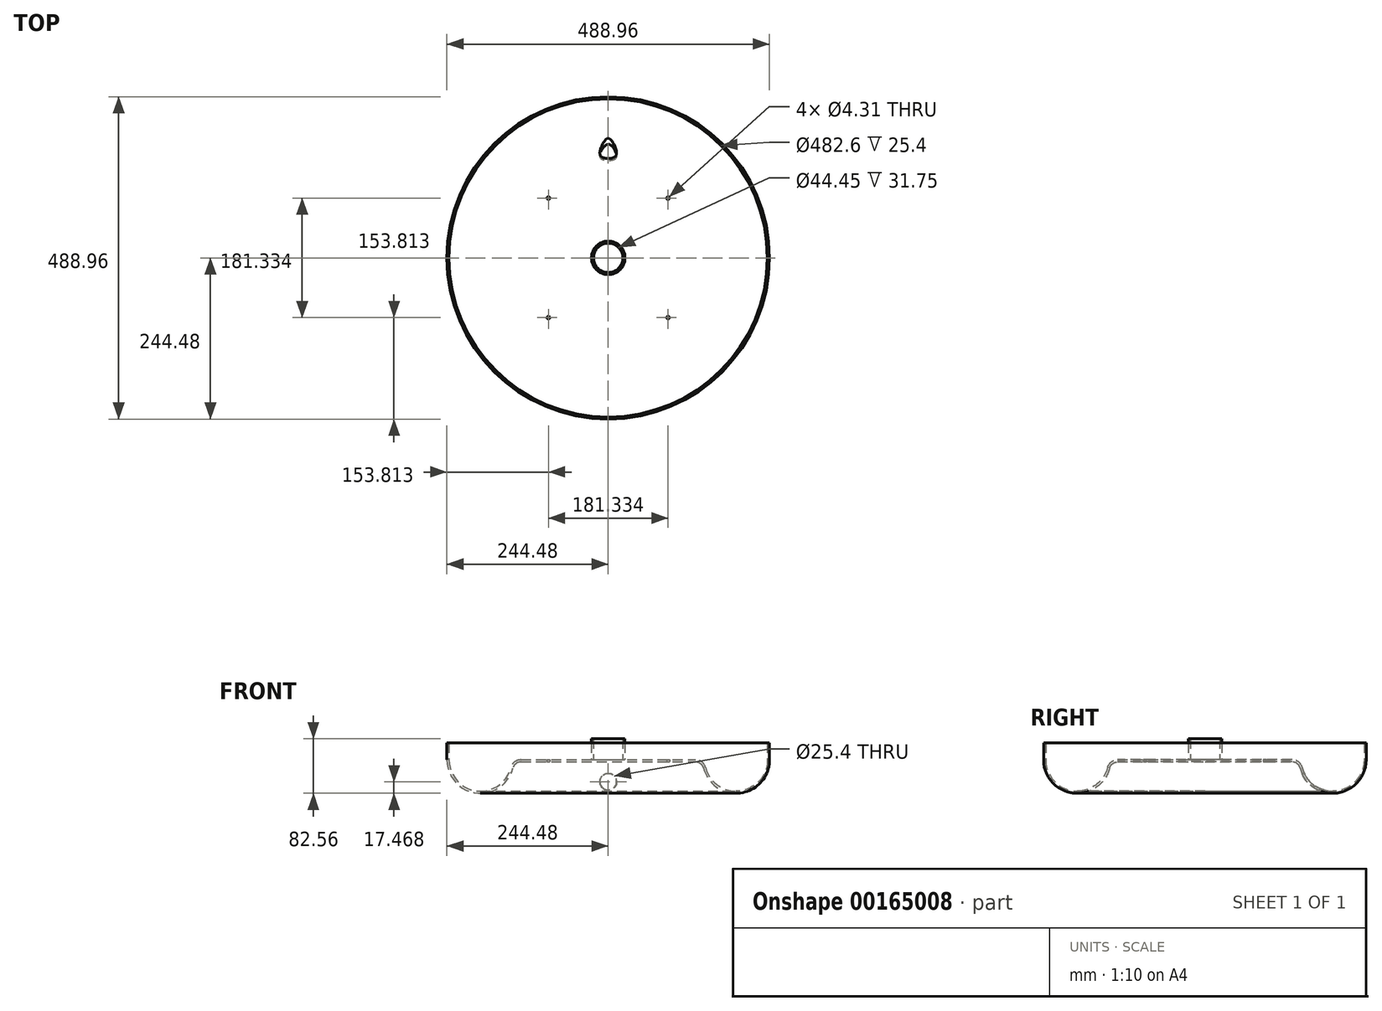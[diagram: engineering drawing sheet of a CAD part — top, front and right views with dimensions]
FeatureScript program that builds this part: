
annotation { "Feature Type Name" : "Feature", "Feature Type Description" : "" }
export const myFeature = defineFeature(function(context is Context, id is Id, definition is map)
    precondition{}
    {
        {
            var Q0;
            Q0=qCreatedBy(makeId("Front.planeOp"),FACE);
            var sketch = newSketch(context, id + "F0", { "sketchPlane" : qUnion([Q0])});
            skLineSegment(sketch, "E0", {"start": v(241.3, 3.17) * mm, "end": v(244.47, 3.17) * mm, "construction": true});
            skArc(sketch, "E1", {"start": v(144.49, -9.53) * mm, "mid": v(139.97, -2.66) * mm, "end": v(132.2, 0) * mm});
            skArc(sketch, "E2", {"start": v(147.56, -8.73) * mm, "mid": v(141.91, -0.15) * mm, "end": v(132.2, 3.17) * mm});
            skLineSegment(sketch, "E3", {"start": v(241.3, 3.17) * mm, "end": v(241.3, 28.58) * mm});
            skLineSegment(sketch, "E4", {"start": v(241.3, 28.58) * mm, "end": v(244.47, 28.58) * mm});
            skLineSegment(sketch, "E5", {"start": v(244.48, 3.17) * mm, "end": v(244.48, 28.58) * mm});
            skArc(sketch, "E6", {"start": v(144.49, -9.53) * mm, "mid": v(200.08, -47.22) * mm, "end": v(244.47, 3.17) * mm});
            skArc(sketch, "E7", {"start": v(147.56, -8.73) * mm, "mid": v(199.68, -44.07) * mm, "end": v(241.3, 3.17) * mm});
            skLineSegment(sketch, "E8.bottom", {"start": v(0, 0) * mm, "end": v(132.2, 0) * mm});
            skLineSegment(sketch, "E8.top", {"start": v(0, 3.17) * mm, "end": v(132.2, 3.17) * mm});
            skLineSegment(sketch, "E8.left", {"start": v(0, 0) * mm, "end": v(0, 3.17) * mm});
            skLineSegment(sketch, "E9", {"start": v(132.2, 3.18) * mm, "end": v(241.3, 3.18) * mm, "construction": true});
            skSolve(sketch);
        }
        {
            var Q0;
            Q0=qCreatedBy(makeId("Top.planeOp"),FACE);
            var sketch = newSketch(context, id + "F1", { "sketchPlane" : qUnion([Q0])});
            skCircle(sketch, "E10", {"center": v(0, 0) * mm, "radius": 25.4 * mm});
            skSolve(sketch);
        }
        {
            var Q0;
            Q0 = qSketchRegion(id + "F0", true);
            var Q1;
            Q1=sQuery(id+"F1.wireOp",EDGE,"E10");
            revolve(context, id + "F2", {"entities" : qUnion([Q0]), "axis" : qUnion([Q1]), "revolveType" : RevolveType.FULL});
        }
        {
            var Q0;
            Q0=qCreatedBy(makeId("Top.planeOp"),FACE);
            cPlane(context, id + "F3", {"entities" : qUnion([Q0]), "cplaneType" : CPlaneType.OFFSET, "offset" : 15.88 * mm, "width" : 152.4 * mm, "height" : 152.4 * mm});
        }
        {
            var Q0;
            Q0=qCreatedBy(id+"F3.planeOp",FACE);
            var sketch = newSketch(context, id + "F4", { "sketchPlane" : qUnion([Q0])});
            skCircle(sketch, "E11", {"center": v(0, 0) * mm, "radius": 25.4 * mm});
            skCircle(sketch, "E12", {"center": v(0, 0) * mm, "radius": 22.23 * mm});
            skSolve(sketch);
        }
        {
            var Q0;
            Q0 = qSketchRegion(id + "F4", true);
            var Q1;
            Q1=makeQuery(id+"F2.opRevolve","SWEPT_FACE",FACE,{"disambiguationData":[OSD([sQuery(id+"F0.wireOp",EDGE,"E8.bottom")])]});
            extrude(context, id + "F5", {"entities" : qUnion([Q0]), "operationType" : NewBodyOperationType.ADD, "depth" : 19.05 * mm, "hasSecondDirection" : true, "secondDirectionBound" : SecondDirectionBoundingType.UP_TO_SURFACE, "secondDirectionOppositeDirection" : true, "secondDirectionBoundEntityFace" : qUnion([Q1]), "secondDirectionDepth" : 25.4 * mm});
        }
        {
            var Q0;
            Q0=qCreatedBy(makeId("Front.planeOp"),FACE);
            var sketch = newSketch(context, id + "F6", { "sketchPlane" : qUnion([Q0])});
            skLineSegment(sketch, "E13", {"start": v(0, 3.17) * mm, "end": v(0, -30.16) * mm, "construction": true});
            skCircle(sketch, "E14", {"center": v(0, -30.16) * mm, "radius": 12.7 * mm});
            skSolve(sketch);
        }
        {
            var Q0;
            Q0 = qSketchRegion(id + "F6", true);
            var Q1;
            Q1=makeQuery(id+"F2.opRevolve","SWEPT_FACE",FACE,{"disambiguationData":[OSD([sQuery(id+"F0.wireOp",EDGE,"E7")])]});
            extrude(context, id + "F7", {"entities" : qUnion([Q0]), "operationType" : NewBodyOperationType.REMOVE, "endBound" : BoundingType.UP_TO_SURFACE, "oppositeDirection" : true, "endBoundEntityFace" : qUnion([Q1]), "depth" : 25.4 * mm});
        }
        {
            var Q0;
            Q0=makeQuery(id+"F2.opRevolve","SWEPT_FACE",FACE,{"disambiguationData":[OSD([sQuery(id+"F0.wireOp",EDGE,"E8.bottom")])]});
            var sketch = newSketch(context, id + "F8", { "sketchPlane" : qUnion([Q0])});
            skLineSegment(sketch, "E15.bottom", {"start": v(-90.67, 90.67) * mm, "end": v(90.67, 90.67) * mm, "construction": true});
            skLineSegment(sketch, "E15.top", {"start": v(-90.67, -90.67) * mm, "end": v(90.67, -90.67) * mm, "construction": true});
            skLineSegment(sketch, "E15.left", {"start": v(-90.67, 90.67) * mm, "end": v(-90.67, -90.67) * mm, "construction": true});
            skLineSegment(sketch, "E15.right", {"start": v(90.67, 90.67) * mm, "end": v(90.67, -90.67) * mm, "construction": true});
            skPoint(sketch, "E15.middle", {"position": v(0, 0) * mm});
            skCircle(sketch, "E16", {"center": v(-90.67, 90.67) * mm, "radius": 3.97 * mm, "construction": true});
            skCircle(sketch, "E17", {"center": v(-90.67, 90.67) * mm, "radius": 2.15 * mm});
            skCircle(sketch, "E18", {"center": v(-90.67, -90.67) * mm, "radius": 2.15 * mm});
            skCircle(sketch, "E19", {"center": v(90.67, -90.67) * mm, "radius": 2.15 * mm});
            skCircle(sketch, "E20", {"center": v(90.67, 90.67) * mm, "radius": 2.15 * mm});
            skSolve(sketch);
        }
        {
            var Q0;
            Q0 = qSketchRegion(id + "F8", true);
            var Q1;
            Q1=makeQuery(id+"F5.boolean.opBoolean","SPLIT",FACE,{"disambiguationData":[TD([makeQuery(id+"F2.opRevolve","SWEPT_FACE",FACE,{"disambiguationData":[OSD([sQuery(id+"F0.wireOp",EDGE,"E2")])]})])],"derivedFrom":makeQuery(id+"F2.opRevolve","SWEPT_FACE",FACE,{"disambiguationData":[OSD([sQuery(id+"F0.wireOp",EDGE,"E8.top")])]})});
            extrude(context, id + "F9", {"entities" : qUnion([Q0]), "operationType" : NewBodyOperationType.REMOVE, "endBound" : BoundingType.UP_TO_SURFACE, "oppositeDirection" : true, "endBoundEntityFace" : qUnion([Q1]), "depth" : 25.4 * mm});
        }
    });
